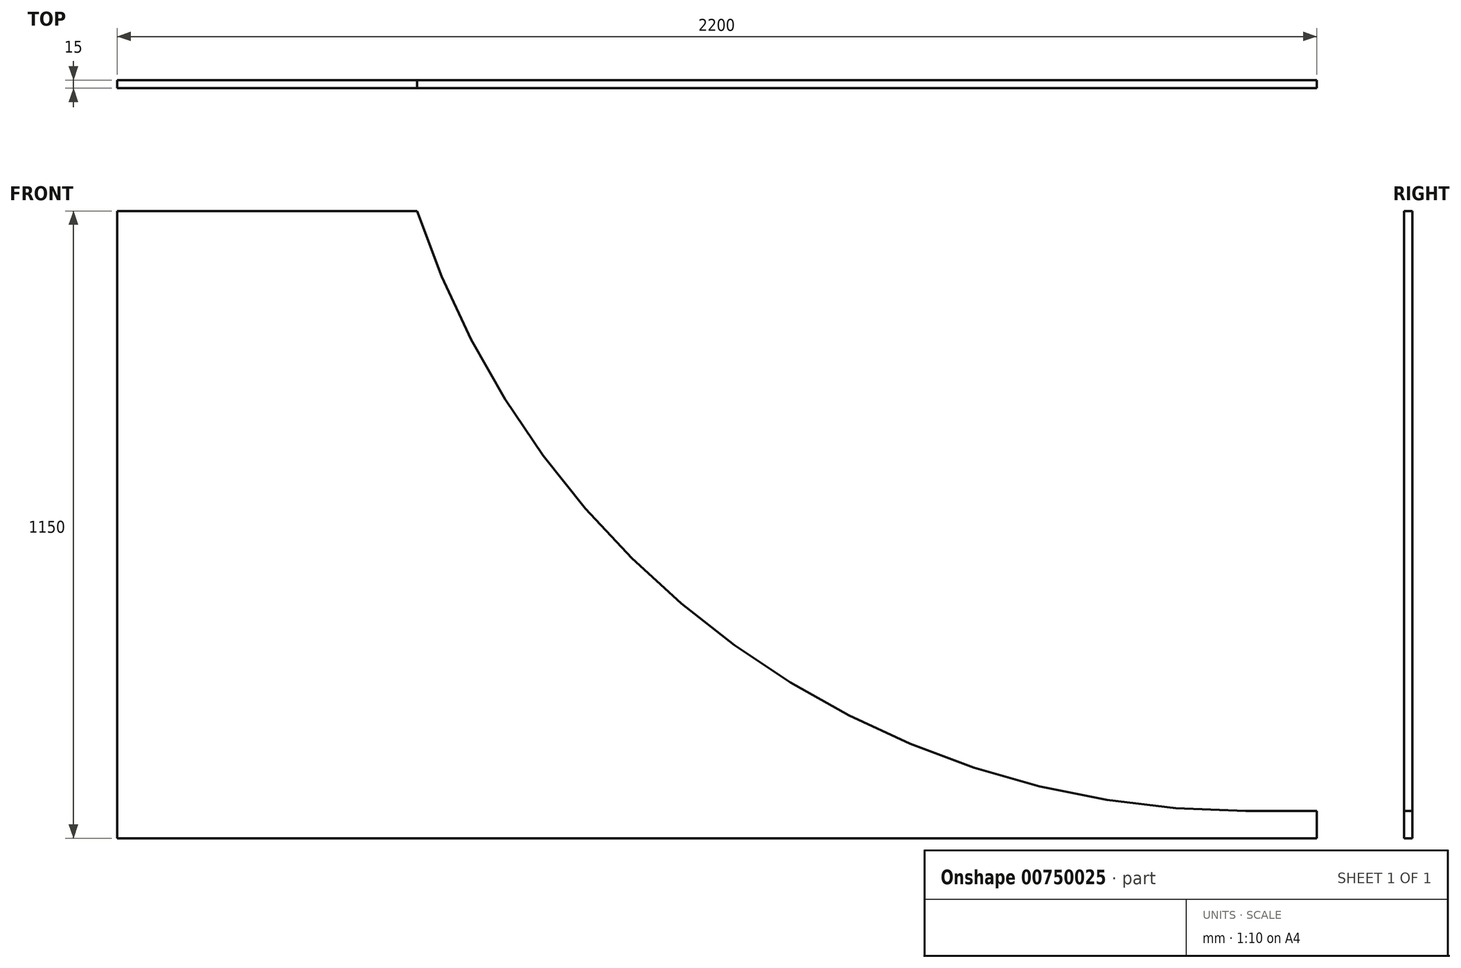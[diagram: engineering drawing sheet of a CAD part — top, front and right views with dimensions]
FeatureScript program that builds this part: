
annotation { "Feature Type Name" : "Feature", "Feature Type Description" : "" }
export const myFeature = defineFeature(function(context is Context, id is Id, definition is map)
    precondition{}
    {
        {
            var Q0;
            Q0=qCreatedBy(makeId("Front.planeOp"),FACE);
            var sketch = newSketch(context, id + "F0", { "sketchPlane" : qUnion([Q0])});
            skLineSegment(sketch, "E0", {"start": v(0, 0) * mm, "end": v(2200, 0) * mm});
            skLineSegment(sketch, "E1", {"start": v(2200, 0) * mm, "end": v(2200, 50) * mm});
            skLineSegment(sketch, "E2", {"start": v(550, 1150) * mm, "end": v(0, 1150) * mm});
            skLineSegment(sketch, "E3", {"start": v(0, 1150) * mm, "end": v(0, 0) * mm});
            skArc(sketch, "E4", {"start": v(550, 1150) * mm, "mid": v(1131.79, 353.85) * mm, "end": v(2069.87, 50) * mm});
            skLineSegment(sketch, "E5", {"start": v(2069.87, 50) * mm, "end": v(2200, 50) * mm});
            skSolve(sketch);
        }
        {
            var Q0;
            Q0 = qSketchRegion(id + "F0", true);
            extrude(context, id + "F1", {"entities" : qUnion([Q0]), "depth" : 15 * mm, "offsetDistance" : 25 * mm});
        }
    });
